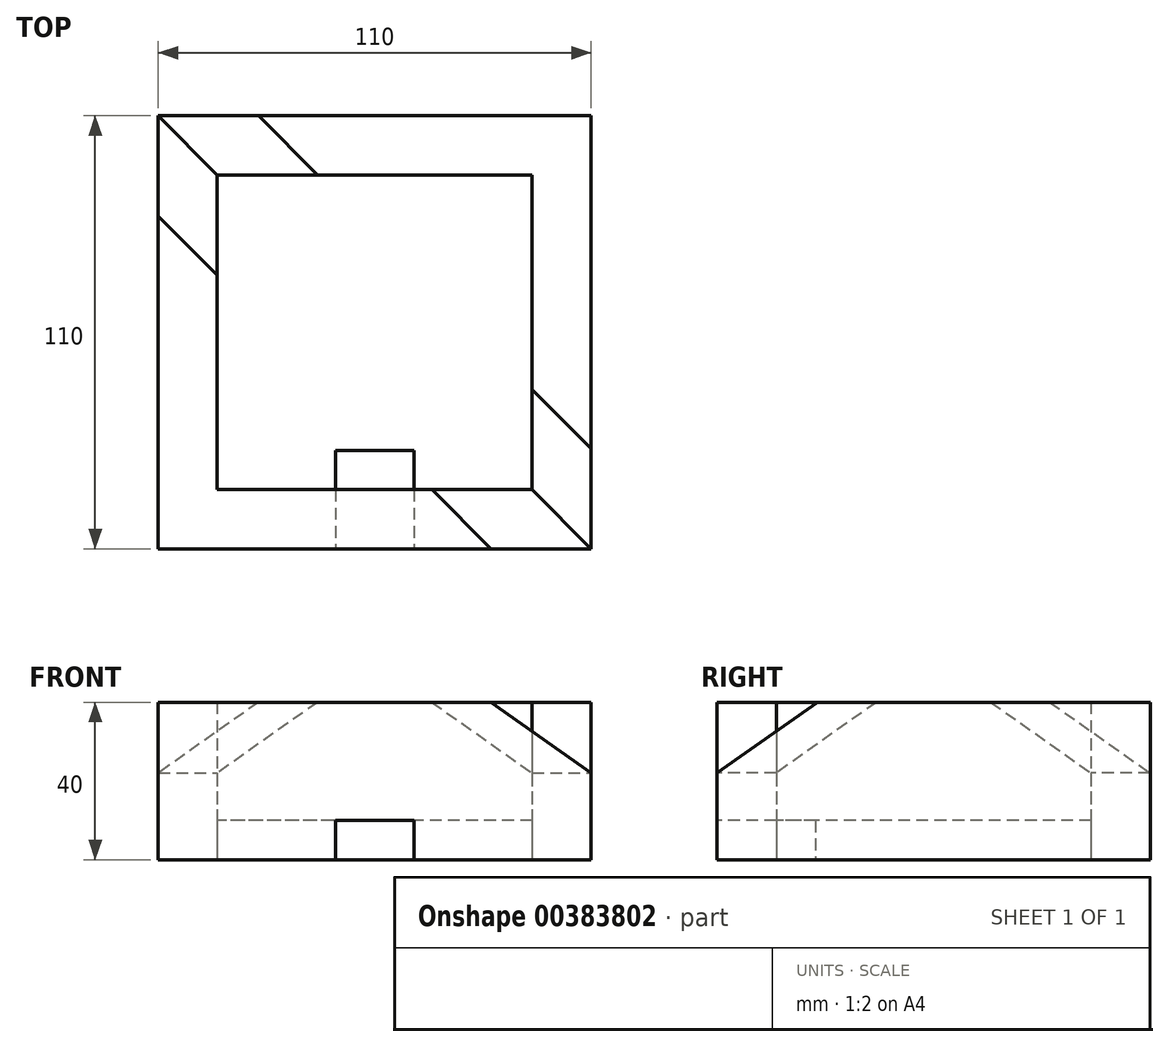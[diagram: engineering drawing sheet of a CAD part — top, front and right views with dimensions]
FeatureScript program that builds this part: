
annotation { "Feature Type Name" : "Feature", "Feature Type Description" : "" }
export const myFeature = defineFeature(function(context is Context, id is Id, definition is map)
    precondition{}
    {
        {
            var Q0;
            Q0=qCreatedBy(makeId("Top.planeOp"),FACE);
            var sketch = newSketch(context, id + "F0", { "sketchPlane" : qUnion([Q0])});
            skLineSegment(sketch, "E0.bottom", {"start": v(35, 35) * mm, "end": v(-35, 35) * mm});
            skLineSegment(sketch, "E0.top", {"start": v(35, -35) * mm, "end": v(-35, -35) * mm});
            skLineSegment(sketch, "E0.left", {"start": v(35, 35) * mm, "end": v(35, -35) * mm});
            skLineSegment(sketch, "E0.right", {"start": v(-35, 35) * mm, "end": v(-35, -35) * mm});
            skPoint(sketch, "E0.middle", {"position": v(0, 0) * mm});
            skLineSegment(sketch, "E1.bottom", {"start": v(40, 40) * mm, "end": v(-40, 40) * mm});
            skLineSegment(sketch, "E1.top", {"start": v(40, -40) * mm, "end": v(-40, -40) * mm});
            skLineSegment(sketch, "E1.left", {"start": v(40, 40) * mm, "end": v(40, -40) * mm});
            skLineSegment(sketch, "E1.right", {"start": v(-40, 40) * mm, "end": v(-40, -40) * mm});
            skLineSegment(sketch, "E2.bottom", {"start": v(55, 55) * mm, "end": v(-55, 55) * mm});
            skLineSegment(sketch, "E2.top", {"start": v(55, -55) * mm, "end": v(-55, -55) * mm});
            skLineSegment(sketch, "E2.left", {"start": v(55, 55) * mm, "end": v(55, -55) * mm});
            skLineSegment(sketch, "E2.right", {"start": v(-55, 55) * mm, "end": v(-55, -55) * mm});
            skSolve(sketch);
        }
        {
            var Q0;
            Q0 = qSketchRegion(id + "F0", true);
            extrude(context, id + "F1", {"entities" : qUnion([Q0]), "depth" : 40 * mm});
        }
        {
            var Q0;
            Q0=makeQuery(id+"F0.imprint","IMPRINT",FACE,{"disambiguationData":[TD([[makeQuery(id+"F0.imprint","IMPRINT",EDGE,{"derivedFrom":sQuery(id+"F0.wireOp",EDGE,"E0.bottom")}),-1.0]])]});
            var Q1;
            Q1=makeQuery(id+"F0.imprint","IMPRINT",FACE,{"disambiguationData":[TD([[makeQuery(id+"F0.imprint","IMPRINT",EDGE,{"derivedFrom":sQuery(id+"F0.wireOp",EDGE,"E0.bottom")}),1.0]])]});
            extrude(context, id + "F2", {"entities" : qUnion([Q0, Q1]), "depth" : 10 * mm});
        }
        {
            var Q0;
            Q0=makeQuery(id+"F1.opExtrude","SWEPT_EDGE",EDGE,{"disambiguationData":[OSD([sQuery(id+"F0.wireOp",EDGE,"E2.top"),sQuery(id+"F0.wireOp",EDGE,"E2.left")])]});
            cPlane(context, id + "F3", {"entities" : qUnion([Q0]), "cplaneType" : CPlaneType.LINE_ANGLE, "offset" : 25 * mm, "angle" : 45 * degree, "width" : 150 * mm, "height" : 150 * mm});
        }
        {
            var Q0;
            Q0=qCreatedBy(id+"F3.planeOp",FACE);
            var sketch = newSketch(context, id + "F4", { "sketchPlane" : qUnion([Q0])});
            skLineSegment(sketch, "E3", {"start": v(0, 0) * mm, "end": v(0, 40) * mm});
            skLineSegment(sketch, "E4", {"start": v(0, 40) * mm, "end": v(-18, 40) * mm});
            skLineSegment(sketch, "E5", {"start": v(0, 40) * mm, "end": v(18, 40) * mm});
            skLineSegment(sketch, "E6", {"start": v(-18, 40) * mm, "end": v(0, 22) * mm});
            skLineSegment(sketch, "E7", {"start": v(0, 40) * mm, "end": v(0, 22) * mm});
            skLineSegment(sketch, "E8", {"start": v(18, 40) * mm, "end": v(0, 22) * mm});
            skSolve(sketch);
        }
        {
            var Q0;
            Q0 = qSketchRegion(id + "F4", true);
            extrude(context, id + "F5", {"entities" : qUnion([Q0]), "operationType" : NewBodyOperationType.REMOVE, "depth" : 200 * mm});
        }
        {
            var Q0;
            Q0=makeQuery(id+"F1.opExtrude","SWEPT_FACE",FACE,{"disambiguationData":[OSD([sQuery(id+"F0.wireOp",EDGE,"E2.top")])]});
            var sketch = newSketch(context, id + "F6", { "sketchPlane" : qUnion([Q0])});
            skLineSegment(sketch, "E9.bottom", {"start": v(10, 10) * mm, "end": v(-10, 10) * mm});
            skLineSegment(sketch, "E9.top", {"start": v(10, -10) * mm, "end": v(-10, -10) * mm});
            skLineSegment(sketch, "E9.left", {"start": v(10, 10) * mm, "end": v(10, -10) * mm});
            skLineSegment(sketch, "E9.right", {"start": v(-10, 10) * mm, "end": v(-10, -10) * mm});
            skPoint(sketch, "E9.middle", {"position": v(0, 0) * mm});
            skSolve(sketch);
        }
        {
            var Q0;
            Q0 = qSketchRegion(id + "F6", true);
            extrude(context, id + "F7", {"entities" : qUnion([Q0]), "operationType" : NewBodyOperationType.REMOVE, "oppositeDirection" : true, "depth" : 25 * mm, "offsetDistance" : 25 * mm});
        }
    });
